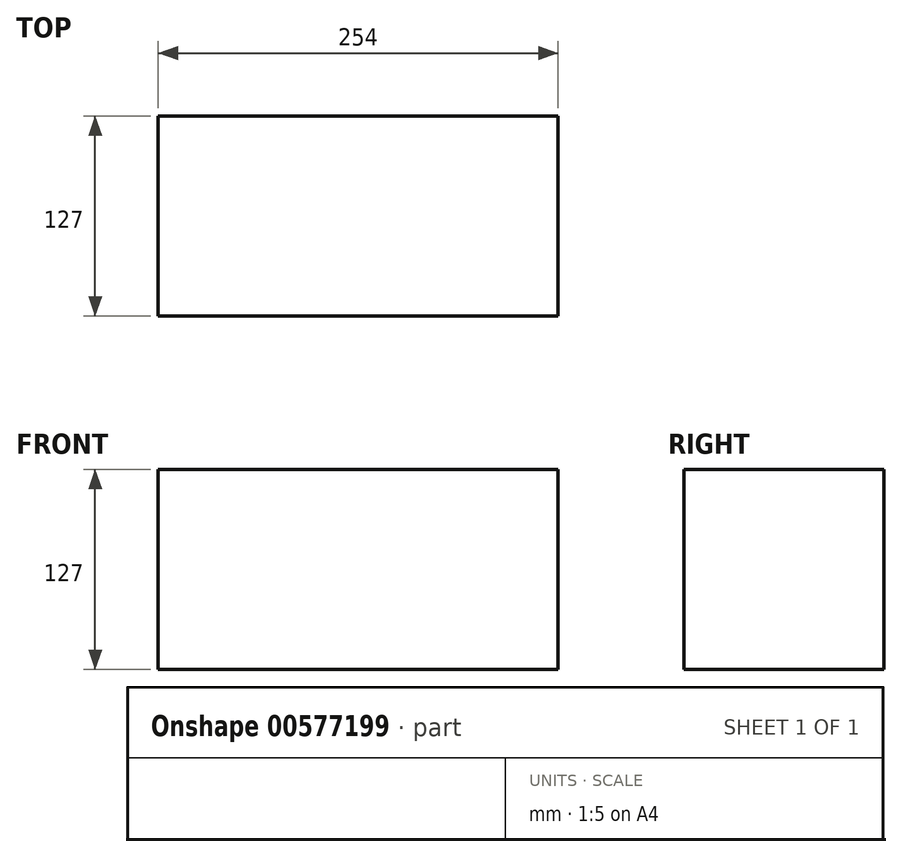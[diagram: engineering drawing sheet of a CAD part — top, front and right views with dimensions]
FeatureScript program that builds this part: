
annotation { "Feature Type Name" : "Feature", "Feature Type Description" : "" }
export const myFeature = defineFeature(function(context is Context, id is Id, definition is map)
    precondition{}
    {
        {
            var Q0;
            Q0=qCreatedBy(makeId("Top.planeOp"),FACE);
            var sketch = newSketch(context, id + "F0", { "sketchPlane" : qUnion([Q0])});
            skLineSegment(sketch, "E0.bottom", {"start": v(0, 0) * mm, "end": v(254, 0) * mm});
            skLineSegment(sketch, "E0.top", {"start": v(0, -127) * mm, "end": v(254, -127) * mm});
            skLineSegment(sketch, "E0.left", {"start": v(0, 0) * mm, "end": v(0, -127) * mm});
            skLineSegment(sketch, "E0.right", {"start": v(254, 0) * mm, "end": v(254, -127) * mm});
            skSolve(sketch);
        }
        {
            var Q0;
            Q0 = qSketchRegion(id + "F0", true);
            extrude(context, id + "F1", {"entities" : qUnion([Q0]), "depth" : 127 * mm, "offsetDistance" : 25.4 * mm});
        }
    });
